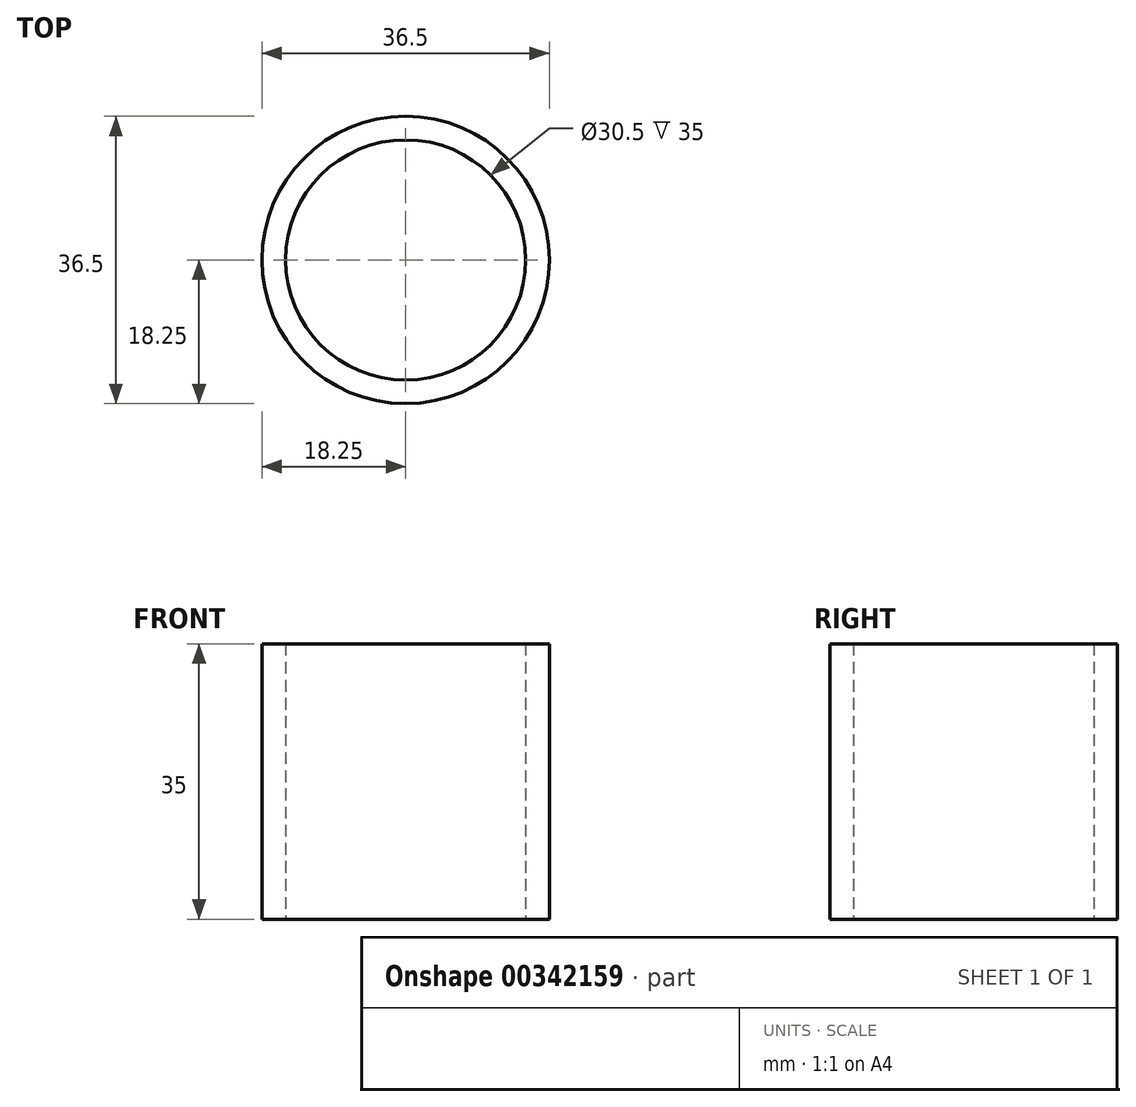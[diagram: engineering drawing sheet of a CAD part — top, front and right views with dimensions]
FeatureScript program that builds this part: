
annotation { "Feature Type Name" : "Feature", "Feature Type Description" : "" }
export const myFeature = defineFeature(function(context is Context, id is Id, definition is map)
    precondition{}
    {
        {
            var Q0;
            Q0=qCreatedBy(makeId("Top.planeOp"),FACE);
            var sketch = newSketch(context, id + "F0", { "sketchPlane" : qUnion([Q0])});
            skCircle(sketch, "E0", {"center": v(0, 0) * mm, "radius": 18.25 * mm});
            skCircle(sketch, "E1", {"center": v(0, 0) * mm, "radius": 15.25 * mm});
            skCircle(sketch, "E2", {"center": v(0, 0) * mm, "radius": 24.6 * mm, "construction": true});
            skSolve(sketch);
        }
        {
            var Q0;
            Q0=qSketchRegion(id+"F0",true);
            var Q1;
            Q1=sQuery(id+"F0.wireOp",EDGE,"E0");
            extrude(context, id + "F1", {"entities" : qUnion([Q0]), "surfaceEntities" : qUnion([Q1]), "endBound" : BoundingType.SYMMETRIC, "depth" : 35 * mm});
        }
    });
